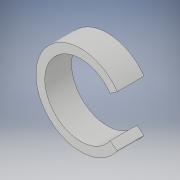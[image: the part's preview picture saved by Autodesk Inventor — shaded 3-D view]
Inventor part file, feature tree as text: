
AUTODESK INVENTOR PART (.ipt)
format: ipt  version: 2017 (Build 210142000, 142)  size: 111,616 bytes
history: native  units: in
note: dims shown in document units (in); Inventor stores cm internally (conversion verified against a paired STEP export)
features: extrude x2, sketch x2
ambient origin geometry x8: Origin, YZ Plane, XZ Plane, XY Plane, X Axis, Y Axis, Z Axis, Center Point
bodies: Solid1 (feature_tree)
feature tree (4):
  extrude  "Extrusion1"  Depth=1.0551in
  extrude  "Extrusion5"  Depth=0.3937in
  sketch  "Sketch1"  dims[d0=1.316in d1=1.0551in]
  sketch  "Sketch5"  dims[d2=0.3937in d3=0.0in d27=0.2405in d28=0.2405in d29=0.3937in d30=0.0in]
